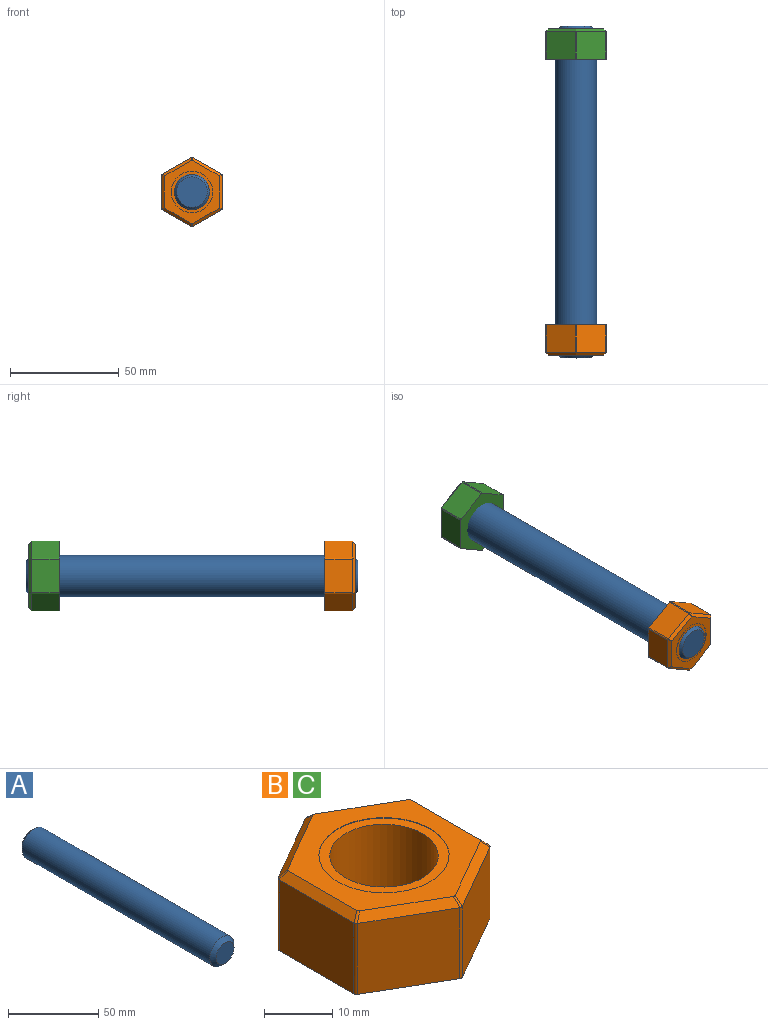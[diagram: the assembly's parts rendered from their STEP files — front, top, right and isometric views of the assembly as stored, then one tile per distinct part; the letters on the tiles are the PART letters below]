
ASSEMBLY  parts=3 mates=2
PART A: 5 faces, bbox 19.1x152.4x19.1 mm
  f0: cylinder r=9.53mm len=147.32mm, axis (0,1,0), area 8816.7mm2, adj f3,f4
  f1: plane 13.97x13.97mm, normal (0,-1,0), area 153.3mm2, adj f4
  f2: plane 13.97x13.97mm, normal (0,1,0), area 153.3mm2, adj f3
  f3: cone r=9.53mm half-angle=45deg, axis (0,-1,0), area 186.3mm2, adj f0,f2
  f4: cone r=6.99mm half-angle=45deg, axis (0,1,0), area 186.3mm2, adj f0,f1
PART B: 29 faces, bbox 27.9x32.1x14 mm
  f0: plane 19.05x19.05mm, normal (0,0,1), area 87.1mm2, adj f2,f9
  f1: plane 32.05x27.93mm, normal (0,0,-1), area 477.5mm2, adj f2,f3,f4,f5,f6,f7,f8,f18
  f2: cylinder r=7.94mm len=15.88mm, axis (0,0,-1), area 692.8mm2, adj f0,f1
  f3: plane 15.39x12.7mm, normal (1,0,0), area 195.5mm2, adj f1,f14,f18,f26
  f4: plane 13.33x12.7mm, normal (0.5,-0.87,0), area 195.5mm2, adj f1,f12,f18,f20
  f5: plane 13.33x12.7mm, normal (-0.5,-0.87,0), area 195.5mm2, adj f1,f11,f20,f22
  f6: plane 15.39x12.7mm, normal (-1,0,0), area 195.5mm2, adj f1,f13,f22,f24
  f7: plane 13.33x12.7mm, normal (-0.5,0.87,0), area 195.5mm2, adj f1,f15,f24,f28
  f8: plane 13.33x12.7mm, normal (0.5,0.87,0), area 195.5mm2, adj f1,f16,f26,f28
  f9: cylinder r=9.53mm len=19.05mm, axis (0,0,-1), area 4.8mm2, adj f0,f10
  f10: plane 29.18x25.39mm, normal (0,0,1), area 273.2mm2, adj f9,f11,f12,f13,f14,f15,f16,f17
  f11: plane 13.51x8.53mm, normal (-0.35,-0.61,0.71), area 26.7mm2, adj f5,f10,f19,f20,f21,f22
  f12: plane 13.51x8.53mm, normal (0.35,-0.61,0.71), area 26.7mm2, adj f4,f10,f17,f18,f19,f20
  f13: plane 15.6x1.27mm, normal (-0.71,0,0.71), area 26.7mm2, adj f6,f10,f21,f22,f23,f24
  f14: plane 15.6x1.27mm, normal (0.71,0,0.71), area 26.7mm2, adj f3,f10,f17,f18,f25,f26
  f15: plane 13.51x8.53mm, normal (-0.35,0.61,0.71), area 26.7mm2, adj f7,f10,f23,f24,f27,f28
  f16: plane 13.51x8.53mm, normal (0.35,0.61,0.71), area 26.7mm2, adj f8,f10,f25,f26,f27,f28
  f17: cylinder r=0.64mm len=1.5mm, axis (0.65,-0.38,-0.65), area 0.9mm2, adj f10,f12,f14,f18
  f18: cylinder r=0.64mm len=12.73mm, axis (0,0,-1), area 8.5mm2, adj f1,f3,f4,f12,f14,f17
  f19: cylinder r=0.64mm len=1.5mm, axis (0,-0.76,-0.65), area 0.9mm2, adj f10,f11,f12,f20
  f20: cylinder r=0.64mm len=12.73mm, axis (0,0,-1), area 8.5mm2, adj f1,f4,f5,f11,f12,f19
  f21: cylinder r=0.64mm len=1.5mm, axis (0.65,0.38,0.65), area 0.9mm2, adj f10,f11,f13,f22
  f22: cylinder r=0.64mm len=12.73mm, axis (0,0,-1), area 8.5mm2, adj f1,f5,f6,f11,f13,f21
  f23: cylinder r=0.64mm len=1.5mm, axis (0.65,-0.38,0.65), area 0.9mm2, adj f10,f13,f15,f24
  f24: cylinder r=0.64mm len=12.73mm, axis (0,0,-1), area 8.5mm2, adj f1,f6,f7,f13,f15,f23
  f25: cylinder r=0.64mm len=1.5mm, axis (0.65,0.38,-0.65), area 0.9mm2, adj f10,f14,f16,f26
  f26: cylinder r=0.64mm len=12.73mm, axis (0,0,-1), area 8.5mm2, adj f1,f3,f8,f14,f16,f25
  f27: cylinder r=0.64mm len=1.5mm, axis (0,-0.76,0.65), area 0.9mm2, adj f10,f15,f16,f28
  f28: cylinder r=0.64mm len=12.73mm, axis (0,0,-1), area 8.5mm2, adj f1,f7,f8,f15,f16,f27
PART C: same geometry as B
PLACE A t=(-12.56,61.15,-11.71)mm
PLACE B rot(axis=(1,0,0),90deg) t=(-12.56,-76.01,-11.71)mm
PLACE C rot(axis=(-1,0,0),90deg) t=(-12.56,45.91,-11.71)mm
MATE fastened C.f2 <-> B.f2  axis (0,-1,0) through (-12.56,45.91,-11.71)mm
MATE fastened B.f2 <-> A.f0  axis (0,1,0) through (-12.56,-76.01,-11.71)mm
